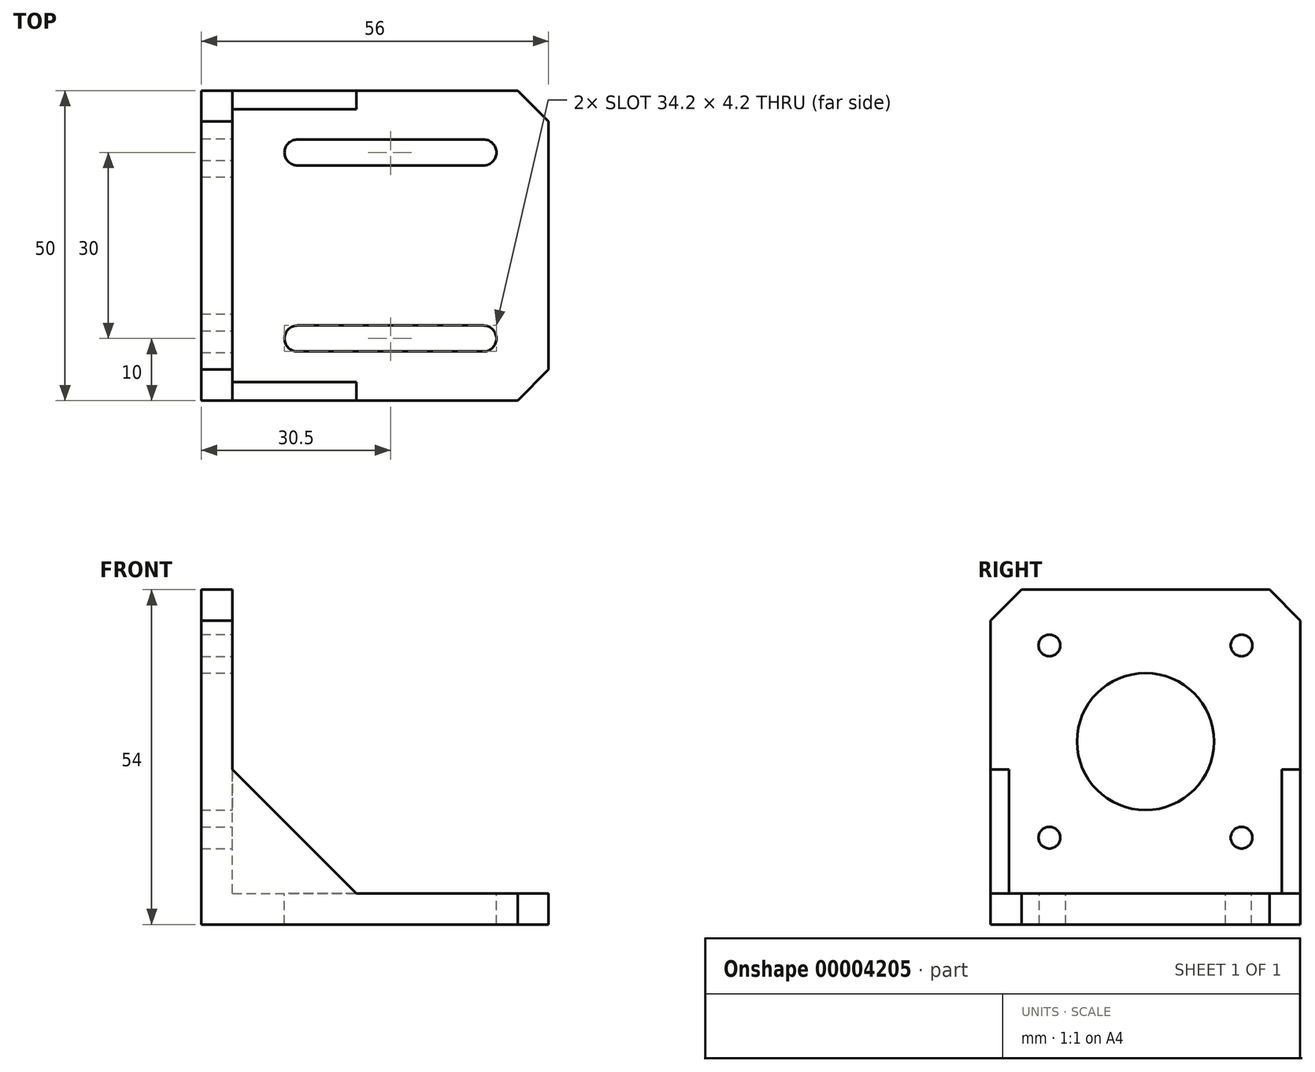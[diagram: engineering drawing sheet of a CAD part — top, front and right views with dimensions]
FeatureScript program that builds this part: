
annotation { "Feature Type Name" : "Feature", "Feature Type Description" : "" }
export const myFeature = defineFeature(function(context is Context, id is Id, definition is map)
    precondition{}
    {
        {
            var Q0;
            Q0=qCreatedBy(makeId("Front.planeOp"),FACE);
            var sketch = newSketch(context, id + "F0", { "sketchPlane" : qUnion([Q0])});
            skLineSegment(sketch, "E0", {"start": v(0, 0) * mm, "end": v(0, 49) * mm});
            skLineSegment(sketch, "E1", {"start": v(0, 0) * mm, "end": v(51, 0) * mm});
            skLineSegment(sketch, "E2.0", {"start": v(-5, 0) * mm, "end": v(-5, 49) * mm});
            skLineSegment(sketch, "E3.0", {"start": v(0, -5) * mm, "end": v(51, -5) * mm});
            skLineSegment(sketch, "E4", {"start": v(0, -5) * mm, "end": v(-5, -5) * mm});
            skLineSegment(sketch, "E5", {"start": v(-5, -5) * mm, "end": v(-5, 0) * mm});
            skLineSegment(sketch, "E6", {"start": v(51, -5) * mm, "end": v(51, 0) * mm});
            skLineSegment(sketch, "E7", {"start": v(-5, 49) * mm, "end": v(0, 49) * mm});
            skSolve(sketch);
        }
        {
            var Q0;
            Q0=makeQuery(id+"F0.imprint","IMPRINT",FACE,{"disambiguationData":[TD([[makeQuery(id+"F0.imprint","IMPRINT",EDGE,{"derivedFrom":sQuery(id+"F0.wireOp",EDGE,"E0")}),1.0]])]});
            extrude(context, id + "F1", {"entities" : qUnion([Q0]), "oppositeDirection" : true, "depth" : 50 * mm});
        }
        {
            var Q0;
            Q0=makeQuery(id+"F1.opExtrude","SWEPT_FACE",FACE,{"disambiguationData":[OSD([sQuery(id+"F0.wireOp",EDGE,"E0")])]});
            var sketch = newSketch(context, id + "F2", { "sketchPlane" : qUnion([Q0])});
            skLineSegment(sketch, "E8", {"start": v(25, 49) * mm, "end": v(25, 0) * mm, "construction": true});
            skLineSegment(sketch, "E9", {"start": v(50, 24.5) * mm, "end": v(0, 24.5) * mm, "construction": true});
            skLineSegment(sketch, "E10.0", {"start": v(50, 40) * mm, "end": v(0, 40) * mm, "construction": true});
            skLineSegment(sketch, "E11.0", {"start": v(50, 9) * mm, "end": v(0, 9) * mm, "construction": true});
            skLineSegment(sketch, "E12.0", {"start": v(9.5, 49) * mm, "end": v(9.5, 0) * mm, "construction": true});
            skLineSegment(sketch, "E13.0", {"start": v(40.5, 49) * mm, "end": v(40.5, 0) * mm, "construction": true});
            skCircle(sketch, "E14", {"center": v(25, 24.5) * mm, "radius": 11.05 * mm});
            skCircle(sketch, "E15", {"center": v(9.5, 40) * mm, "radius": 1.75 * mm});
            skCircle(sketch, "E16", {"center": v(40.5, 40) * mm, "radius": 1.75 * mm});
            skCircle(sketch, "E17", {"center": v(40.5, 9) * mm, "radius": 1.75 * mm});
            skCircle(sketch, "E18", {"center": v(9.5, 9) * mm, "radius": 1.75 * mm});
            skSolve(sketch);
        }
        {
            var Q0;
            {Q0=qUnion([makeQuery(id+"F2.imprint","IMPRINT",FACE,{"disambiguationData":[TD([[makeQuery(id+"F2.imprint","IMPRINT",EDGE,{"derivedFrom":sQuery(id+"F2.wireOp",EDGE,"E14")}),1.0]])]}),makeQuery(id+"F2.imprint","IMPRINT",FACE,{"disambiguationData":[TD([[makeQuery(id+"F2.imprint","IMPRINT",EDGE,{"derivedFrom":sQuery(id+"F2.wireOp",EDGE,"E15")}),1.0]])]}),makeQuery(id+"F2.imprint","IMPRINT",FACE,{"disambiguationData":[TD([[makeQuery(id+"F2.imprint","IMPRINT",EDGE,{"derivedFrom":sQuery(id+"F2.wireOp",EDGE,"E16")}),1.0]])]}),makeQuery(id+"F2.imprint","IMPRINT",FACE,{"disambiguationData":[TD([[makeQuery(id+"F2.imprint","IMPRINT",EDGE,{"derivedFrom":sQuery(id+"F2.wireOp",EDGE,"E17")}),1.0]])]}),makeQuery(id+"F2.imprint","IMPRINT",FACE,{"disambiguationData":[TD([[makeQuery(id+"F2.imprint","IMPRINT",EDGE,{"derivedFrom":sQuery(id+"F2.wireOp",EDGE,"E18")}),1.0]])]})]);}
            extrude(context, id + "F3", {"entities" : qUnion([Q0]), "operationType" : NewBodyOperationType.REMOVE, "oppositeDirection" : true, "depth" : 25 * mm});
        }
        {
            var Q0;
            Q0=makeQuery(id+"F1.opExtrude","SWEPT_FACE",FACE,{"disambiguationData":[OSD([sQuery(id+"F0.wireOp",EDGE,"E1")])]});
            var sketch = newSketch(context, id + "F4", { "sketchPlane" : qUnion([Q0])});
            skLineSegment(sketch, "E19", {"start": v(51, 25) * mm, "end": v(0, 25) * mm, "construction": true});
            skLineSegment(sketch, "E20", {"start": v(25.5, 50) * mm, "end": v(25.5, 0) * mm, "construction": true});
            skLineSegment(sketch, "E21.0", {"start": v(10.5, 50) * mm, "end": v(10.5, 0) * mm, "construction": true});
            skLineSegment(sketch, "E22.0", {"start": v(40.5, 50) * mm, "end": v(40.5, 0) * mm, "construction": true});
            skLineSegment(sketch, "E23.0", {"start": v(51, 40) * mm, "end": v(0, 40) * mm, "construction": true});
            skLineSegment(sketch, "E24.0", {"start": v(51, 10) * mm, "end": v(0, 10) * mm, "construction": true});
            skLineSegment(sketch, "E25.0", {"start": v(40.5, 42.1) * mm, "end": v(10.5, 42.1) * mm});
            skLineSegment(sketch, "E26.0", {"start": v(40.5, 37.9) * mm, "end": v(10.5, 37.9) * mm});
            skLineSegment(sketch, "E27.0", {"start": v(40.5, 12.1) * mm, "end": v(10.5, 12.1) * mm});
            skLineSegment(sketch, "E28.0", {"start": v(40.5, 7.9) * mm, "end": v(10.5, 7.9) * mm});
            skArc(sketch, "E29", {"start": v(10.5, 42.1) * mm, "mid": v(8.4, 40) * mm, "end": v(10.5, 37.9) * mm});
            skArc(sketch, "E30", {"start": v(40.5, 37.9) * mm, "mid": v(42.6, 40) * mm, "end": v(40.5, 42.1) * mm});
            skArc(sketch, "E31", {"start": v(40.5, 7.9) * mm, "mid": v(42.6, 10) * mm, "end": v(40.5, 12.1) * mm});
            skArc(sketch, "E32", {"start": v(10.5, 12.1) * mm, "mid": v(8.4, 10) * mm, "end": v(10.5, 7.9) * mm});
            skSolve(sketch);
        }
        {
            var Q0;
            Q0=makeQuery(id+"F4.imprint","IMPRINT",FACE,{"disambiguationData":[TD([[makeQuery(id+"F4.imprint","IMPRINT",EDGE,{"derivedFrom":sQuery(id+"F4.wireOp",EDGE,"E25.0")}),1.0]])]});
            var Q1;
            Q1=makeQuery(id+"F4.imprint","IMPRINT",FACE,{"disambiguationData":[TD([[makeQuery(id+"F4.imprint","IMPRINT",EDGE,{"derivedFrom":sQuery(id+"F4.wireOp",EDGE,"E27.0")}),1.0]])]});
            extrude(context, id + "F5", {"entities" : qUnion([Q0, Q1]), "operationType" : NewBodyOperationType.REMOVE, "oppositeDirection" : true, "depth" : 25 * mm});
        }
        {
            var Q0;
            Q0=makeQuery(id+"F1.opExtrude","CAP_EDGE",EDGE,{"disambiguationData":[OSD([sQuery(id+"F0.wireOp",EDGE,"E7")])],"isStart":false});
            var Q1;
            Q1=makeQuery(id+"F1.opExtrude","CAP_EDGE",EDGE,{"disambiguationData":[OSD([sQuery(id+"F0.wireOp",EDGE,"E7")])],"isStart":true});
            var Q2;
            Q2=makeQuery(id+"F1.opExtrude","CAP_EDGE",EDGE,{"disambiguationData":[OSD([sQuery(id+"F0.wireOp",EDGE,"E6")])],"isStart":false});
            var Q3;
            Q3=makeQuery(id+"F1.opExtrude","CAP_EDGE",EDGE,{"disambiguationData":[OSD([sQuery(id+"F0.wireOp",EDGE,"E6")])],"isStart":true});
            chamfer(context, id + "F6", {"entities" : qUnion([Q0, Q1, Q2, Q3]), "width" : 5 * mm, "tangentPropagation" : true});
        }
        {
            var Q0;
            Q0=makeQuery(id+"F1.opExtrude","CAP_FACE",FACE,{"disambiguationData":[OSD([sQuery(id+"F0.wireOp",EDGE,"E0"),sQuery(id+"F0.wireOp",EDGE,"E1"),sQuery(id+"F0.wireOp",EDGE,"E2.0"),sQuery(id+"F0.wireOp",EDGE,"E4"),sQuery(id+"F0.wireOp",EDGE,"E6"),sQuery(id+"F0.wireOp",EDGE,"E7")])],"isStart":true});
            var sketch = newSketch(context, id + "F7", { "sketchPlane" : qUnion([Q0])});
            skLineSegment(sketch, "E33", {"start": v(0, 0) * mm, "end": v(-26.23, 0) * mm, "construction": true});
            skLineSegment(sketch, "E34", {"start": v(0, 0) * mm, "end": v(0, -19.06) * mm, "construction": true});
            skLineSegment(sketch, "E35", {"start": v(0, 20) * mm, "end": v(20, 0) * mm});
            skSolve(sketch);
        }
        {
            var Q0;
            {var subQ1=sQuery(id+"F7.wireOp",EDGE,"E35");Q0=makeQuery(id+"F7.imprint","IMPRINT",FACE,{"disambiguationData":[TD([[makeQuery(id+"F7.imprint","IMPRINT",EDGE,{"derivedFrom":subQ1}),-1.0]])]});}
            extrude(context, id + "F8", {"entities" : qUnion([Q0]), "operationType" : NewBodyOperationType.ADD, "oppositeDirection" : true, "depth" : 3 * mm});
        }
        {
            var Q0;
            Q0=makeQuery(id+"F1.opExtrude","CAP_FACE",FACE,{"disambiguationData":[OSD([sQuery(id+"F0.wireOp",EDGE,"E0"),sQuery(id+"F0.wireOp",EDGE,"E1"),sQuery(id+"F0.wireOp",EDGE,"E2.0"),sQuery(id+"F0.wireOp",EDGE,"E4"),sQuery(id+"F0.wireOp",EDGE,"E6"),sQuery(id+"F0.wireOp",EDGE,"E7")])],"isStart":false});
            var sketch = newSketch(context, id + "F9", { "sketchPlane" : qUnion([Q0])});
            skLineSegment(sketch, "E36", {"start": v(0, 0) * mm, "end": v(17.94, 0) * mm, "construction": true});
            skLineSegment(sketch, "E37", {"start": v(0, 0) * mm, "end": v(0, -17.04) * mm, "construction": true});
            skLineSegment(sketch, "E38", {"start": v(0, 20) * mm, "end": v(-20, 0) * mm});
            skSolve(sketch);
        }
        {
            var Q0;
            {var subQ1=sQuery(id+"F9.wireOp",EDGE,"E38");Q0=makeQuery(id+"F9.imprint","IMPRINT",FACE,{"disambiguationData":[TD([[makeQuery(id+"F9.imprint","IMPRINT",EDGE,{"derivedFrom":subQ1}),1.0]])]});}
            extrude(context, id + "F10", {"entities" : qUnion([Q0]), "operationType" : NewBodyOperationType.ADD, "oppositeDirection" : true, "depth" : 3 * mm});
        }
    });
